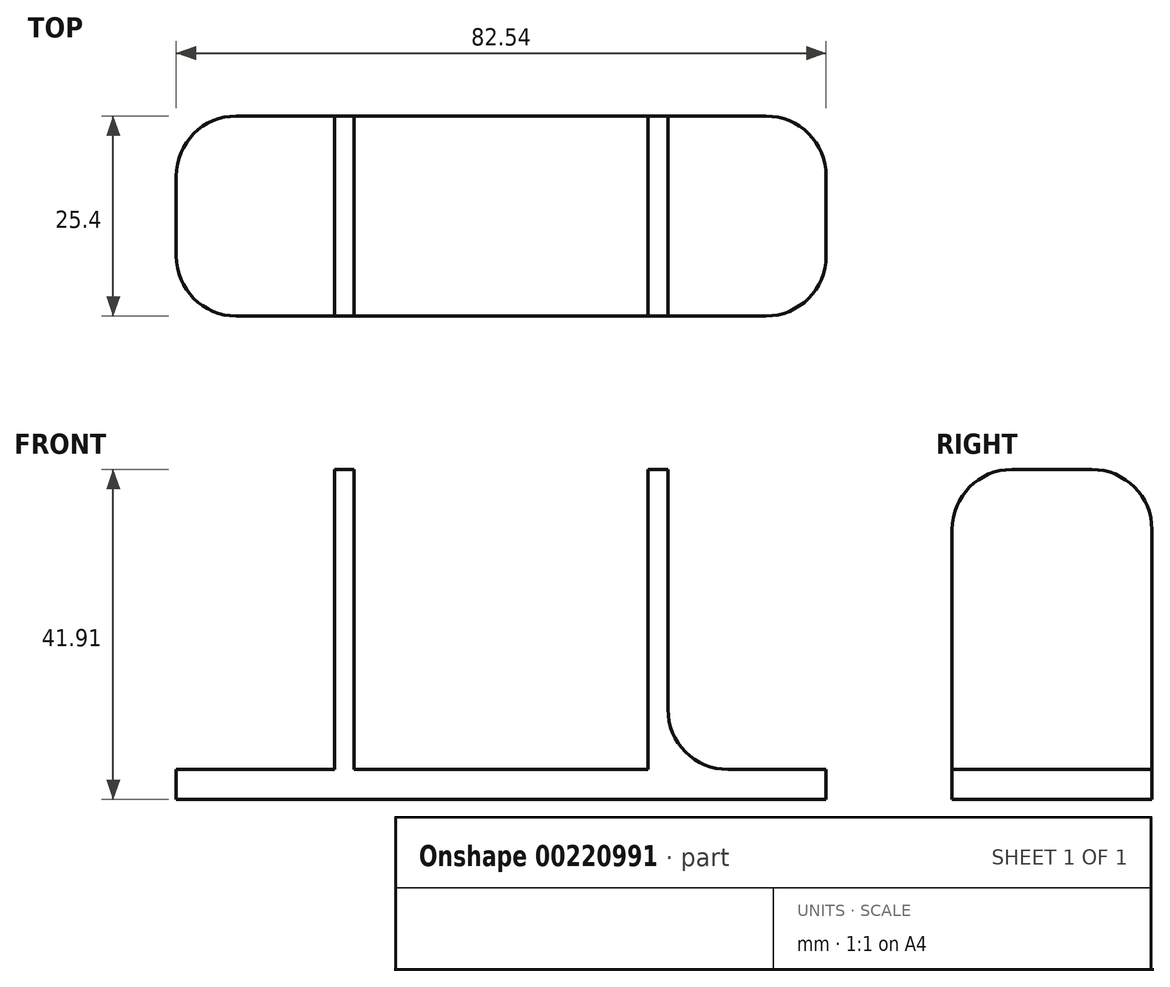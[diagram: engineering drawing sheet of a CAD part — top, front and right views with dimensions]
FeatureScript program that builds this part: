
annotation { "Feature Type Name" : "Feature", "Feature Type Description" : "" }
export const myFeature = defineFeature(function(context is Context, id is Id, definition is map)
    precondition{}
    {
        {
            var Q0;
            Q0=qCreatedBy(makeId("Top.planeOp"),FACE);
            var sketch = newSketch(context, id + "F0", { "sketchPlane" : qUnion([Q0])});
            skLineSegment(sketch, "E0.bottom", {"start": v(41.28, 12.7) * mm, "end": v(-41.28, 12.7) * mm});
            skLineSegment(sketch, "E0.top", {"start": v(41.28, -12.7) * mm, "end": v(-41.28, -12.7) * mm});
            skLineSegment(sketch, "E0.left", {"start": v(41.28, 12.7) * mm, "end": v(41.28, -12.7) * mm});
            skLineSegment(sketch, "E0.right", {"start": v(-41.28, 12.7) * mm, "end": v(-41.28, -12.7) * mm});
            skPoint(sketch, "E0.middle", {"position": v(0, 0) * mm});
            skSolve(sketch);
        }
        {
            var Q0;
            Q0 = qSketchRegion(id + "F0", true);
            extrude(context, id + "F1", {"entities" : qUnion([Q0]), "depth" : 3.8 * mm});
        }
        {
            var Q0;
            Q0=makeQuery(id+"F1.opExtrude","CAP_FACE",FACE,{"disambiguationData":[OSD([sQuery(id+"F0.wireOp",EDGE,"E0.bottom"),sQuery(id+"F0.wireOp",EDGE,"E0.top"),sQuery(id+"F0.wireOp",EDGE,"E0.left"),sQuery(id+"F0.wireOp",EDGE,"E0.right")])],"isStart":false});
            var sketch = newSketch(context, id + "F2", { "sketchPlane" : qUnion([Q0])});
            skLineSegment(sketch, "E1.bottom", {"start": v(-21.2, 12.7) * mm, "end": v(-18.65, 12.7) * mm});
            skLineSegment(sketch, "E1.top", {"start": v(-21.2, -12.7) * mm, "end": v(-18.65, -12.7) * mm});
            skLineSegment(sketch, "E1.left", {"start": v(-21.2, 12.7) * mm, "end": v(-21.2, -12.7) * mm});
            skLineSegment(sketch, "E1.right", {"start": v(-18.65, 12.7) * mm, "end": v(-18.65, -12.7) * mm});
            skLineSegment(sketch, "E2.bottom", {"start": v(18.65, 12.7) * mm, "end": v(21.2, 12.7) * mm});
            skLineSegment(sketch, "E2.top", {"start": v(18.65, -12.7) * mm, "end": v(21.2, -12.7) * mm});
            skLineSegment(sketch, "E2.left", {"start": v(18.65, 12.7) * mm, "end": v(18.65, -12.7) * mm});
            skLineSegment(sketch, "E2.right", {"start": v(21.2, 12.7) * mm, "end": v(21.2, -12.7) * mm});
            skSolve(sketch);
        }
        {
            var Q0;
            Q0 = qSketchRegion(id + "F2", true);
            extrude(context, id + "F3", {"entities" : qUnion([Q0]), "operationType" : NewBodyOperationType.ADD, "depth" : 38.1 * mm});
        }
        {
            var Q0;
            Q0=makeQuery(id+"F1.opExtrude","SWEPT_EDGE",EDGE,{"disambiguationData":[OSD([sQuery(id+"F0.wireOp",EDGE,"E0.bottom"),sQuery(id+"F0.wireOp",EDGE,"E0.right")])]});
            var Q1;
            Q1=makeQuery(id+"F1.opExtrude","SWEPT_EDGE",EDGE,{"disambiguationData":[OSD([sQuery(id+"F0.wireOp",EDGE,"E0.top"),sQuery(id+"F0.wireOp",EDGE,"E0.right")])]});
            var Q2;
            Q2=makeQuery(id+"F1.opExtrude","SWEPT_EDGE",EDGE,{"disambiguationData":[OSD([sQuery(id+"F0.wireOp",EDGE,"E0.bottom"),sQuery(id+"F0.wireOp",EDGE,"E0.left")])]});
            var Q3;
            Q3=makeQuery(id+"F1.opExtrude","SWEPT_EDGE",EDGE,{"disambiguationData":[OSD([sQuery(id+"F0.wireOp",EDGE,"E0.top"),sQuery(id+"F0.wireOp",EDGE,"E0.left")])]});
            var Q4;
            Q4=makeQuery(id+"F3.opExtrude","CAP_EDGE",EDGE,{"disambiguationData":[OSD([sQuery(id+"F2.wireOp",EDGE,"E1.left")])],"isStart":true});
            var Q5;
            Q5=makeQuery(id+"F3.opExtrude","CAP_EDGE",EDGE,{"disambiguationData":[OSD([sQuery(id+"F2.wireOp",EDGE,"E2.right")])],"isStart":true});
            var Q6;
            Q6=makeQuery(id+"F3.opExtrude","CAP_EDGE",EDGE,{"disambiguationData":[OSD([sQuery(id+"F2.wireOp",EDGE,"E2.bottom")])],"isStart":false});
            var Q7;
            Q7=makeQuery(id+"F3.opExtrude","CAP_EDGE",EDGE,{"disambiguationData":[OSD([sQuery(id+"F2.wireOp",EDGE,"E1.bottom")])],"isStart":false});
            var Q8;
            Q8=makeQuery(id+"F3.opExtrude","CAP_EDGE",EDGE,{"disambiguationData":[OSD([sQuery(id+"F2.wireOp",EDGE,"E1.top")])],"isStart":false});
            var Q9;
            Q9=makeQuery(id+"F3.opExtrude","CAP_EDGE",EDGE,{"disambiguationData":[OSD([sQuery(id+"F2.wireOp",EDGE,"E2.top")])],"isStart":false});
            fillet(context, id + "F4", {"entities" : qUnion([Q0, Q1, Q2, Q3, Q4, Q5, Q6, Q7, Q8, Q9]), "radius" : 7.62 * mm, "tangentPropagation" : true, "allowEdgeOverflow" : false});
        }
    });
